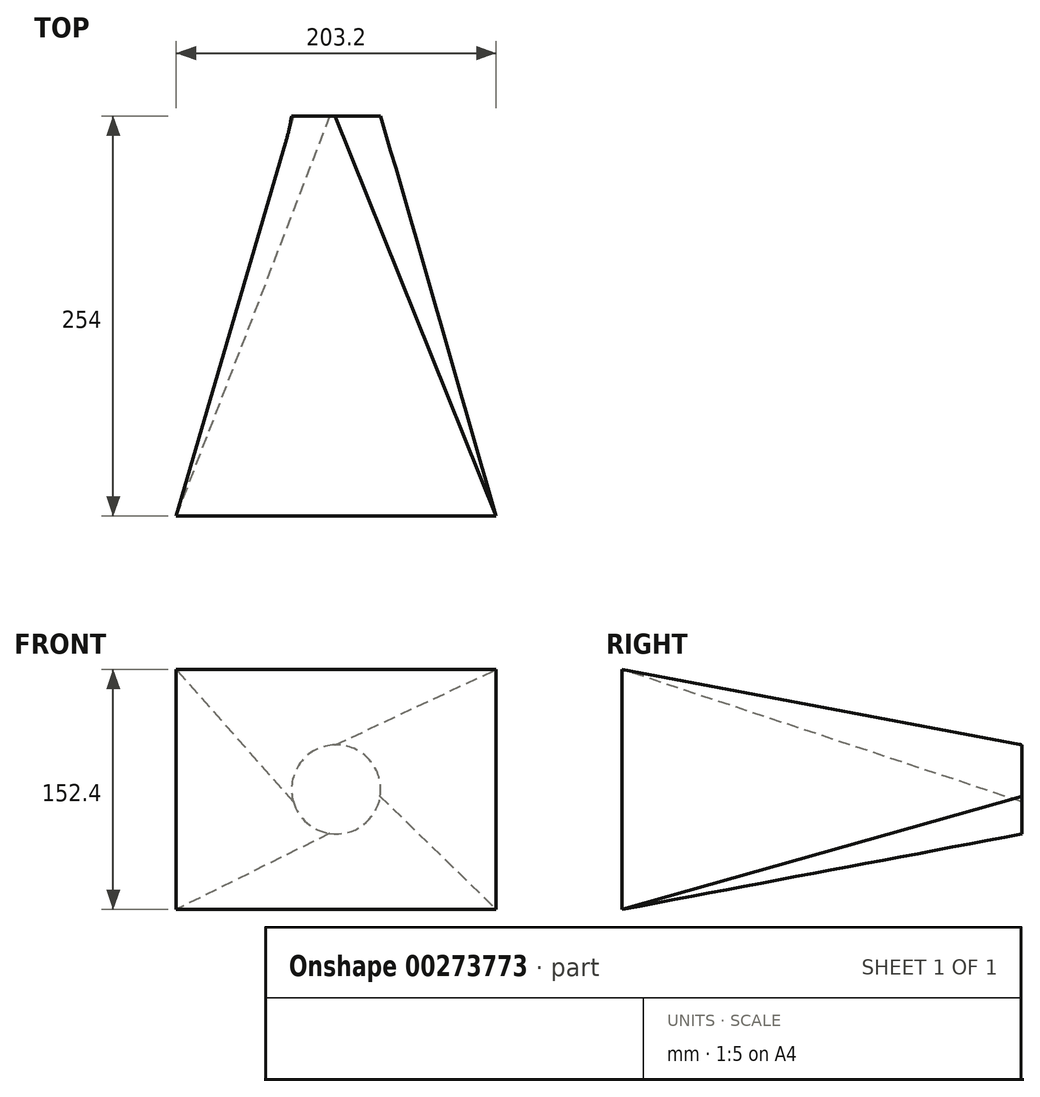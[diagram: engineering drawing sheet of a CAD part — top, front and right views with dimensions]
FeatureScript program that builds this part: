
annotation { "Feature Type Name" : "Feature", "Feature Type Description" : "" }
export const myFeature = defineFeature(function(context is Context, id is Id, definition is map)
    precondition{}
    {
        {
            var Q0;
            Q0=qCreatedBy(makeId("Front.planeOp"),FACE);
            cPlane(context, id + "F0", {"entities" : qUnion([Q0]), "cplaneType" : CPlaneType.OFFSET, "offset" : 254 * mm, "width" : 152.4 * mm, "height" : 152.4 * mm});
        }
        {
            var Q0;
            Q0=qCreatedBy(makeId("Front.planeOp"),FACE);
            var sketch = newSketch(context, id + "F1", { "sketchPlane" : qUnion([Q0])});
            skArc(sketch, "E0", {"start": v(-0.59, 28.3) * mm, "mid": v(-22.8, 16.76) * mm, "end": v(-27.18, -7.9) * mm});
            skArc(sketch, "E1", {"start": v(-27.18, -7.9) * mm, "mid": v(-18.6, -21.34) * mm, "end": v(-4.1, -28) * mm});
            skArc(sketch, "E2", {"start": v(27.97, -4.3) * mm, "mid": v(21.29, 18.65) * mm, "end": v(-0.59, 28.3) * mm});
            skArc(sketch, "E3", {"start": v(-4.1, -28) * mm, "mid": v(16.82, -22.76) * mm, "end": v(27.97, -4.3) * mm});
            skSolve(sketch);
        }
        {
            var Q0;
            Q0=qCreatedBy(id+"F0.planeOp",FACE);
            var sketch = newSketch(context, id + "F2", { "sketchPlane" : qUnion([Q0])});
            skLineSegment(sketch, "E4.bottom", {"start": v(101.6, -76.2) * mm, "end": v(-101.6, -76.2) * mm});
            skLineSegment(sketch, "E4.top", {"start": v(101.6, 76.2) * mm, "end": v(-101.6, 76.2) * mm});
            skLineSegment(sketch, "E4.left", {"start": v(101.6, -76.2) * mm, "end": v(101.6, 76.2) * mm});
            skLineSegment(sketch, "E4.right", {"start": v(-101.6, -76.2) * mm, "end": v(-101.6, 76.2) * mm});
            skPoint(sketch, "E4.middle", {"position": v(0, 0) * mm});
            skSolve(sketch);
        }
        {
            var Q0;
            Q0=makeQuery(id+"F1.imprint","IMPRINT",FACE,{"disambiguationData":[TD([[makeQuery(id+"F1.imprint","IMPRINT",EDGE,{"derivedFrom":sQuery(id+"F1.wireOp",EDGE,"E0")}),1.0]])]});
            var Q1;
            Q1=makeQuery(id+"F2.imprint","IMPRINT",FACE,{"disambiguationData":[TD([[makeQuery(id+"F2.imprint","IMPRINT",EDGE,{"derivedFrom":sQuery(id+"F2.wireOp",EDGE,"E4.bottom")}),-1.0]])]});
            loft(context, id + "F3", {"sheetProfilesArray" : [{ "sheetProfileEntities" : qUnion([Q0]) }, { "sheetProfileEntities" : qUnion([Q1]) }]});
        }
    });
